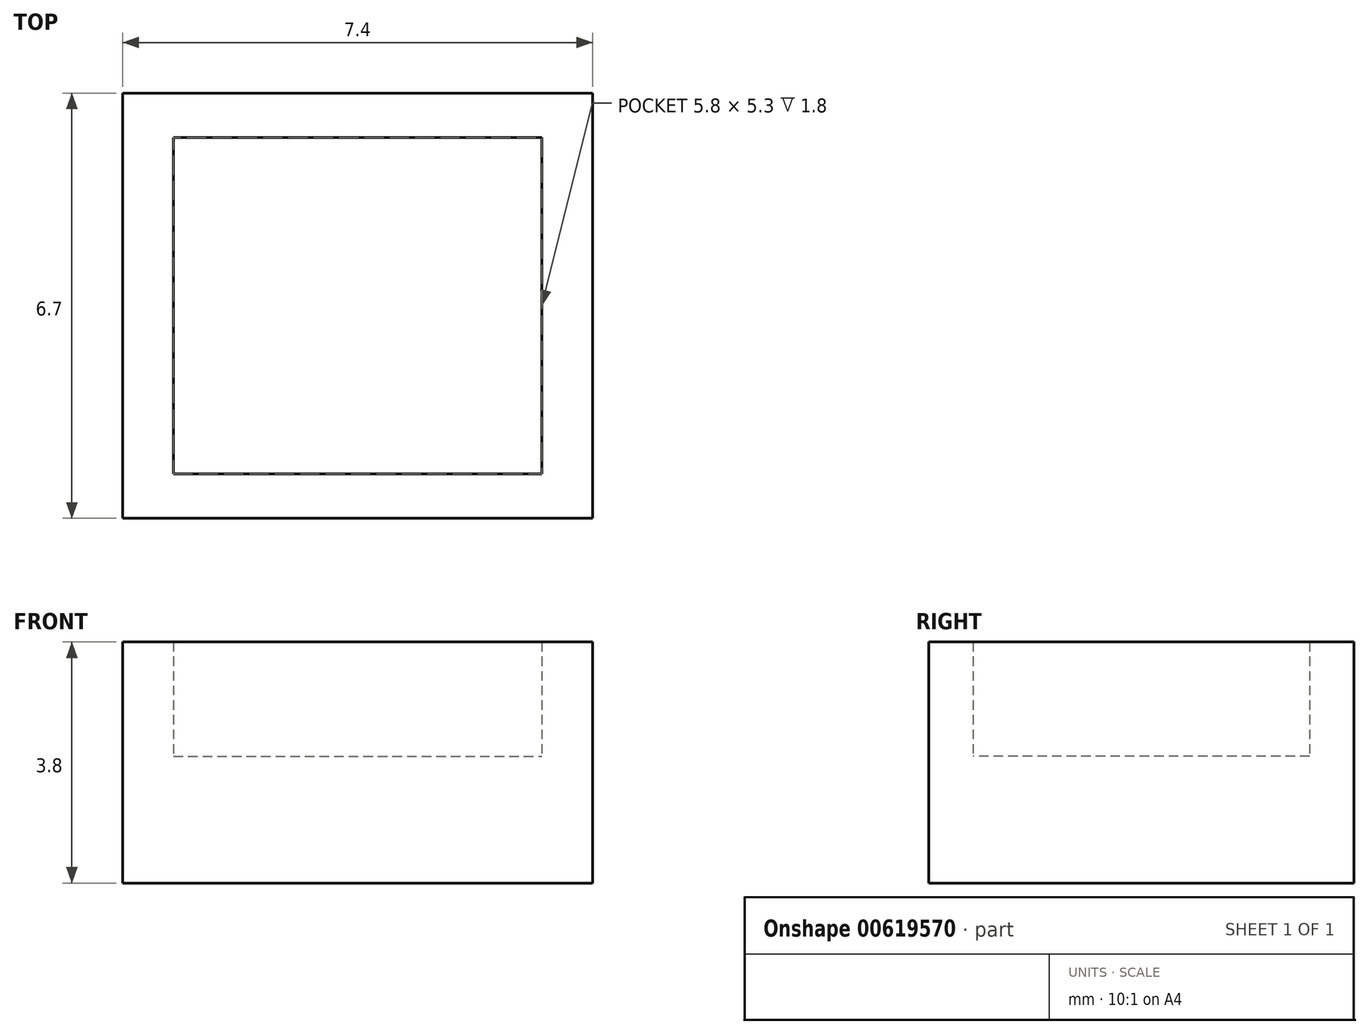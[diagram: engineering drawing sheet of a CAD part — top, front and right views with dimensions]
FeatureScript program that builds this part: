
annotation { "Feature Type Name" : "Feature", "Feature Type Description" : "" }
export const myFeature = defineFeature(function(context is Context, id is Id, definition is map)
    precondition{}
    {
        {
            var Q0;
            Q0=qCreatedBy(makeId("Top.planeOp"),FACE);
            var sketch = newSketch(context, id + "F0", { "sketchPlane" : qUnion([Q0])});
            skLineSegment(sketch, "E0.bottom", {"start": v(-2.9, 2.65) * mm, "end": v(2.9, 2.65) * mm});
            skLineSegment(sketch, "E0.top", {"start": v(-2.9, -2.65) * mm, "end": v(2.9, -2.65) * mm});
            skLineSegment(sketch, "E0.left", {"start": v(-2.9, 2.65) * mm, "end": v(-2.9, -2.65) * mm});
            skLineSegment(sketch, "E0.right", {"start": v(2.9, 2.65) * mm, "end": v(2.9, -2.65) * mm});
            skLineSegment(sketch, "E1.bottom", {"start": v(-3.7, 3.35) * mm, "end": v(3.7, 3.35) * mm});
            skLineSegment(sketch, "E1.top", {"start": v(-3.7, -3.35) * mm, "end": v(3.7, -3.35) * mm});
            skLineSegment(sketch, "E1.left", {"start": v(-3.7, 3.35) * mm, "end": v(-3.7, -3.35) * mm});
            skLineSegment(sketch, "E1.right", {"start": v(3.7, 3.35) * mm, "end": v(3.7, -3.35) * mm});
            skLineSegment(sketch, "E2", {"start": v(-3.7, 3.35) * mm, "end": v(0, 0) * mm, "construction": true});
            skSolve(sketch);
        }
        {
            var Q0;
            Q0 = qSketchRegion(id + "F0", true);
            var Q1;
            Q1=makeQuery(id+"F0.imprint","IMPRINT",FACE,{"disambiguationData":[TD([[makeQuery(id+"F0.imprint","IMPRINT",EDGE,{"derivedFrom":sQuery(id+"F0.wireOp",EDGE,"DWUxgoPM-gqFy-f02u-0Bdt-RgcddomFzFik.bottom")}),-1.0]])]});
            var Q2;
            Q2=makeQuery(id+"F0.imprint","IMPRINT",FACE,{"disambiguationData":[TD([[makeQuery(id+"F0.imprint","IMPRINT",EDGE,{"derivedFrom":sQuery(id+"F0.wireOp",EDGE,"nFwJT2V7-7BPN-cpks-yOcO-u6HSCKIUvoVJ.bottom")}),1.0]])]});
            extrude(context, id + "F1", {"entities" : qUnion([Q0, Q1, Q2]), "depth" : 1.8 * mm, "offsetDistance" : 25 * mm});
        }
        {
            var Q0;
            Q0=makeQuery(id+"F1.opExtrude","CAP_FACE",FACE,{"disambiguationData":[OSD([sQuery(id+"F0.wireOp",EDGE,"E0.bottom"),sQuery(id+"F0.wireOp",EDGE,"E0.top"),sQuery(id+"F0.wireOp",EDGE,"E0.left"),sQuery(id+"F0.wireOp",EDGE,"E0.right"),sQuery(id+"F0.wireOp",EDGE,"E1.bottom"),sQuery(id+"F0.wireOp",EDGE,"E1.top"),sQuery(id+"F0.wireOp",EDGE,"E1.left"),sQuery(id+"F0.wireOp",EDGE,"E1.right")])],"isStart":true});
            var sketch = newSketch(context, id + "F2", { "sketchPlane" : qUnion([Q0])});
            skLineSegment(sketch, "E3.bottom", {"start": v(-3.7, 3.35) * mm, "end": v(3.7, 3.35) * mm});
            skLineSegment(sketch, "E3.top", {"start": v(-3.7, -3.35) * mm, "end": v(3.7, -3.35) * mm});
            skLineSegment(sketch, "E3.left", {"start": v(-3.7, 3.35) * mm, "end": v(-3.7, -3.35) * mm});
            skLineSegment(sketch, "E3.right", {"start": v(3.7, 3.35) * mm, "end": v(3.7, -3.35) * mm});
            skSolve(sketch);
        }
        {
            var Q0;
            Q0 = qSketchRegion(id + "F2", true);
            extrude(context, id + "F3", {"entities" : qUnion([Q0]), "operationType" : NewBodyOperationType.ADD, "depth" : 2 * mm, "offsetDistance" : 25 * mm});
        }
    });
